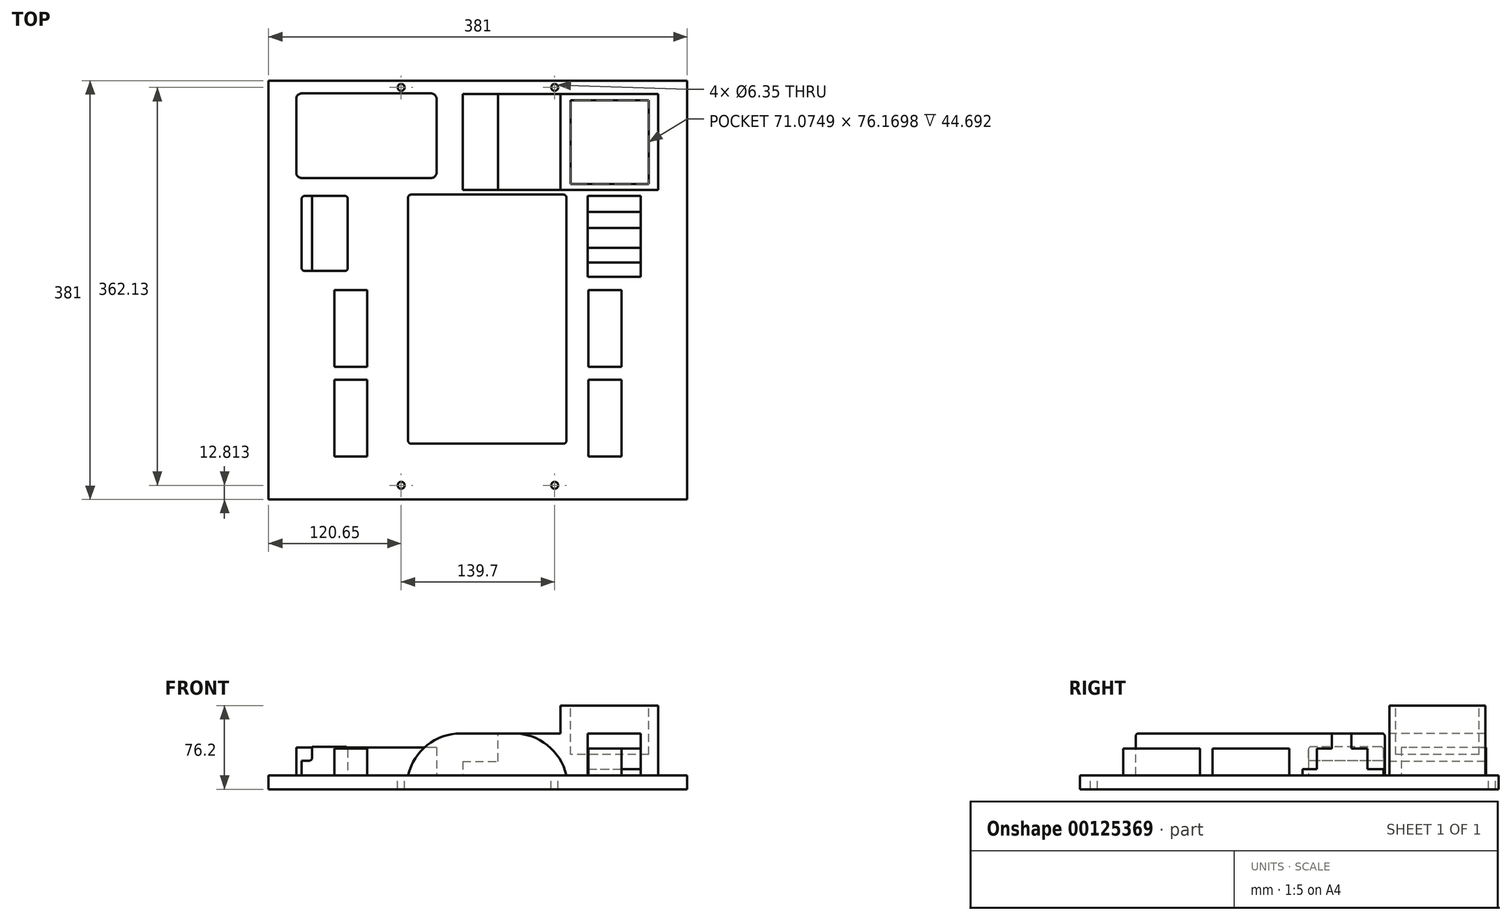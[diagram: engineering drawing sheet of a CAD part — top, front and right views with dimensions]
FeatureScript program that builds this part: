
annotation { "Feature Type Name" : "Feature", "Feature Type Description" : "" }
export const myFeature = defineFeature(function(context is Context, id is Id, definition is map)
    precondition{}
    {
        {
            var Q0;
            Q0=qCreatedBy(makeId("Top.planeOp"),FACE);
            var sketch = newSketch(context, id + "F0", { "sketchPlane" : qUnion([Q0])});
            skLineSegment(sketch, "E0.bottom", {"start": v(190.5, 190.5) * mm, "end": v(-190.5, 190.5) * mm});
            skLineSegment(sketch, "E0.top", {"start": v(190.5, -190.5) * mm, "end": v(-190.5, -190.5) * mm});
            skLineSegment(sketch, "E0.left", {"start": v(190.5, 190.5) * mm, "end": v(190.5, -190.5) * mm});
            skLineSegment(sketch, "E0.right", {"start": v(-190.5, 190.5) * mm, "end": v(-190.5, -190.5) * mm});
            skPoint(sketch, "E0.middle", {"position": v(0, 0) * mm});
            skSolve(sketch);
        }
        {
            var Q0;
            Q0=makeQuery(id+"F0.imprint","IMPRINT",FACE,{"disambiguationData":[TD([[makeQuery(id+"F0.imprint","IMPRINT",EDGE,{"derivedFrom":sQuery(id+"F0.wireOp",EDGE,"E0.bottom")}),1.0]])]});
            extrude(context, id + "F1", {"entities" : qUnion([Q0]), "depth" : 12.7 * mm});
        }
        {
            var Q0;
            Q0=makeQuery(id+"F1.opExtrude","CAP_FACE",FACE,{"disambiguationData":[OSD([sQuery(id+"F0.wireOp",EDGE,"E0.bottom"),sQuery(id+"F0.wireOp",EDGE,"E0.top"),sQuery(id+"F0.wireOp",EDGE,"E0.left"),sQuery(id+"F0.wireOp",EDGE,"E0.right")])],"isStart":false});
            var sketch = newSketch(context, id + "F2", { "sketchPlane" : qUnion([Q0])});
            skSolve(sketch);
        }
        {
            var Q0;
            Q0=makeQuery(id+"F2.imprint","IMPRINT",FACE,{"disambiguationData":[TD([[makeQuery(id+"F2.imprint","IMPRINT",EDGE,{"derivedFrom":makeQuery(id+"F1.opExtrude","CAP_EDGE",EDGE,{"disambiguationData":[OSD([sQuery(id+"F0.wireOp",EDGE,"E0.bottom")])],"isStart":false})}),1.0]])]});
            var sketch = newSketch(context, id + "F3", { "sketchPlane" : qUnion([Q0])});
            skLineSegment(sketch, "E1.bottom", {"start": v(-63.5, -139.7) * mm, "end": v(80.52, -139.7) * mm});
            skLineSegment(sketch, "E1.top", {"start": v(-63.5, 86.87) * mm, "end": v(80.52, 86.87) * mm});
            skLineSegment(sketch, "E1.left", {"start": v(-63.5, -139.7) * mm, "end": v(-63.5, 86.87) * mm});
            skLineSegment(sketch, "E1.right", {"start": v(80.52, -139.7) * mm, "end": v(80.52, 86.87) * mm});
            skSolve(sketch);
        }
        {
            var Q0;
            Q0=makeQuery(id+"F3.imprint","IMPRINT",FACE,{"disambiguationData":[TD([[makeQuery(id+"F3.imprint","IMPRINT",EDGE,{"derivedFrom":sQuery(id+"F3.wireOp",EDGE,"E1.bottom")}),1.0]])]});
            extrude(context, id + "F4", {"entities" : qUnion([Q0]), "operationType" : NewBodyOperationType.ADD, "depth" : 38.1 * mm});
        }
        {
            var Q0;
            Q0=makeQuery(id+"F2.imprint","IMPRINT",FACE,{"disambiguationData":[TD([[makeQuery(id+"F2.imprint","IMPRINT",EDGE,{"derivedFrom":makeQuery(id+"F1.opExtrude","CAP_EDGE",EDGE,{"disambiguationData":[OSD([sQuery(id+"F0.wireOp",EDGE,"E0.bottom")])],"isStart":false})}),1.0]])]});
            var sketch = newSketch(context, id + "F5", { "sketchPlane" : qUnion([Q0])});
            skLineSegment(sketch, "E2.bottom", {"start": v(-13.9, 178.37) * mm, "end": v(164.16, 178.37) * mm});
            skLineSegment(sketch, "E2.top", {"start": v(-13.9, 91) * mm, "end": v(164.16, 91) * mm});
            skLineSegment(sketch, "E2.left", {"start": v(-13.9, 178.37) * mm, "end": v(-13.9, 91) * mm});
            skLineSegment(sketch, "E2.right", {"start": v(164.16, 178.37) * mm, "end": v(164.16, 91) * mm});
            skSolve(sketch);
        }
        {
            var Q0;
            Q0 = qSketchRegion(id + "F5", true);
            extrude(context, id + "F6", {"entities" : qUnion([Q0]), "operationType" : NewBodyOperationType.ADD, "depth" : 63.5 * mm});
        }
        {
            var Q0;
            Q0=makeQuery(id+"F2.imprint","IMPRINT",FACE,{"disambiguationData":[TD([[makeQuery(id+"F2.imprint","IMPRINT",EDGE,{"derivedFrom":makeQuery(id+"F1.opExtrude","CAP_EDGE",EDGE,{"disambiguationData":[OSD([sQuery(id+"F0.wireOp",EDGE,"E0.bottom")])],"isStart":false})}),1.0]])]});
            var sketch = newSketch(context, id + "F7", { "sketchPlane" : qUnion([Q0])});
            skLineSegment(sketch, "E3.bottom", {"start": v(-37.6, 178.96) * mm, "end": v(-165.35, 178.96) * mm});
            skLineSegment(sketch, "E3.top", {"start": v(-37.6, 102) * mm, "end": v(-165.35, 102) * mm});
            skLineSegment(sketch, "E3.left", {"start": v(-37.6, 178.96) * mm, "end": v(-37.6, 102) * mm});
            skLineSegment(sketch, "E3.right", {"start": v(-165.35, 178.96) * mm, "end": v(-165.35, 102) * mm});
            skSolve(sketch);
        }
        {
            var Q0;
            Q0 = qSketchRegion(id + "F7", true);
            extrude(context, id + "F8", {"entities" : qUnion([Q0]), "operationType" : NewBodyOperationType.ADD, "depth" : 25.15 * mm});
        }
        {
            var Q0;
            Q0=makeQuery(id+"F2.imprint","IMPRINT",FACE,{"disambiguationData":[TD([[makeQuery(id+"F2.imprint","IMPRINT",EDGE,{"derivedFrom":makeQuery(id+"F1.opExtrude","CAP_EDGE",EDGE,{"disambiguationData":[OSD([sQuery(id+"F0.wireOp",EDGE,"E0.bottom")])],"isStart":false})}),1.0]])]});
            var sketch = newSketch(context, id + "F9", { "sketchPlane" : qUnion([Q0])});
            skLineSegment(sketch, "E4.bottom", {"start": v(-160.35, 85.65) * mm, "end": v(-118.44, 85.65) * mm});
            skLineSegment(sketch, "E4.top", {"start": v(-160.35, 17.48) * mm, "end": v(-118.44, 17.48) * mm});
            skLineSegment(sketch, "E4.left", {"start": v(-160.35, 85.65) * mm, "end": v(-160.35, 17.48) * mm});
            skLineSegment(sketch, "E4.right", {"start": v(-118.44, 85.65) * mm, "end": v(-118.44, 17.48) * mm});
            skSolve(sketch);
        }
        {
            var Q0;
            Q0 = qSketchRegion(id + "F9", true);
            extrude(context, id + "F10", {"entities" : qUnion([Q0]), "operationType" : NewBodyOperationType.ADD, "depth" : 26.03 * mm});
        }
        {
            var Q0;
            Q0=makeQuery(id+"F2.imprint","IMPRINT",FACE,{"disambiguationData":[TD([[makeQuery(id+"F2.imprint","IMPRINT",EDGE,{"derivedFrom":makeQuery(id+"F1.opExtrude","CAP_EDGE",EDGE,{"disambiguationData":[OSD([sQuery(id+"F0.wireOp",EDGE,"E0.bottom")])],"isStart":false})}),1.0]])]});
            var sketch = newSketch(context, id + "F11", { "sketchPlane" : qUnion([Q0])});
            skLineSegment(sketch, "E5.bottom", {"start": v(99.83, 85.66) * mm, "end": v(148, 85.66) * mm});
            skLineSegment(sketch, "E5.top", {"start": v(99.83, 12) * mm, "end": v(148, 12) * mm});
            skLineSegment(sketch, "E5.left", {"start": v(99.83, 85.66) * mm, "end": v(99.83, 12) * mm});
            skLineSegment(sketch, "E5.right", {"start": v(148, 85.66) * mm, "end": v(148, 12) * mm});
            skSolve(sketch);
        }
        {
            var Q0;
            Q0 = qSketchRegion(id + "F11", true);
            extrude(context, id + "F12", {"entities" : qUnion([Q0]), "operationType" : NewBodyOperationType.ADD, "depth" : 38.1 * mm});
        }
        {
            var Q0;
            Q0=makeQuery(id+"F2.imprint","IMPRINT",FACE,{"disambiguationData":[TD([[makeQuery(id+"F2.imprint","IMPRINT",EDGE,{"derivedFrom":makeQuery(id+"F1.opExtrude","CAP_EDGE",EDGE,{"disambiguationData":[OSD([sQuery(id+"F0.wireOp",EDGE,"E0.bottom")])],"isStart":false})}),1.0]])]});
            var sketch = newSketch(context, id + "F13", { "sketchPlane" : qUnion([Q0])});
            skLineSegment(sketch, "E6.bottom", {"start": v(-130.73, 0) * mm, "end": v(-100.64, 0) * mm});
            skLineSegment(sketch, "E6.top", {"start": v(-130.73, -69.85) * mm, "end": v(-100.64, -69.85) * mm});
            skLineSegment(sketch, "E6.left", {"start": v(-130.73, 0) * mm, "end": v(-130.73, -69.85) * mm});
            skLineSegment(sketch, "E6.right", {"start": v(-100.64, 0) * mm, "end": v(-100.64, -69.85) * mm});
            skLineSegment(sketch, "E7.bottom", {"start": v(-130.73, -81.45) * mm, "end": v(-100.64, -81.45) * mm});
            skLineSegment(sketch, "E7.top", {"start": v(-130.73, -151.3) * mm, "end": v(-100.64, -151.3) * mm});
            skLineSegment(sketch, "E7.left", {"start": v(-130.73, -81.45) * mm, "end": v(-130.73, -151.3) * mm});
            skLineSegment(sketch, "E7.right", {"start": v(-100.64, -81.45) * mm, "end": v(-100.64, -151.3) * mm});
            skLineSegment(sketch, "E8.MirrorCS", {"start": v(100.64, 0) * mm, "end": v(100.64, -69.85) * mm});
            skLineSegment(sketch, "E9.MirrorCS", {"start": v(130.73, 0) * mm, "end": v(100.64, 0) * mm});
            skLineSegment(sketch, "E10.MirrorCS", {"start": v(130.73, 0) * mm, "end": v(130.73, -69.85) * mm});
            skLineSegment(sketch, "E11.MirrorCS", {"start": v(130.73, -69.85) * mm, "end": v(100.64, -69.85) * mm});
            skLineSegment(sketch, "E12.MirrorCS", {"start": v(130.73, -81.45) * mm, "end": v(100.64, -81.45) * mm});
            skLineSegment(sketch, "E13.MirrorCS", {"start": v(130.73, -81.45) * mm, "end": v(130.73, -151.3) * mm});
            skLineSegment(sketch, "E14.MirrorCS", {"start": v(130.73, -151.3) * mm, "end": v(100.64, -151.3) * mm});
            skLineSegment(sketch, "E15.MirrorCS", {"start": v(100.64, -81.45) * mm, "end": v(100.64, -151.3) * mm});
            skSolve(sketch);
        }
        {
            var Q0;
            Q0 = qSketchRegion(id + "F13", true);
            extrude(context, id + "F14", {"entities" : qUnion([Q0]), "operationType" : NewBodyOperationType.ADD, "depth" : 24.38 * mm});
        }
        {
            var Q0;
            Q0=makeQuery(id+"F4.opExtrude","CAP_EDGE",EDGE,{"disambiguationData":[OSD([sQuery(id+"F3.wireOp",EDGE,"E1.right")])],"isStart":false});
            var Q1;
            Q1=makeQuery(id+"F4.opExtrude","CAP_EDGE",EDGE,{"disambiguationData":[OSD([sQuery(id+"F3.wireOp",EDGE,"E1.left")])],"isStart":false});
            fillet(context, id + "F15", {"entities" : qUnion([Q0, Q1]), "radius" : 49.26 * mm, "tangentPropagation" : true, "allowEdgeOverflow" : false});
        }
        {
            var Q0;
            Q0=makeQuery(id+"F6.opExtrude","CAP_FACE",FACE,{"disambiguationData":[OSD([sQuery(id+"F5.wireOp",EDGE,"E2.bottom"),sQuery(id+"F5.wireOp",EDGE,"E2.top"),sQuery(id+"F5.wireOp",EDGE,"E2.left"),sQuery(id+"F5.wireOp",EDGE,"E2.right")])],"isStart":false});
            var sketch = newSketch(context, id + "F16", { "sketchPlane" : qUnion([Q0])});
            skLineSegment(sketch, "E16.bottom", {"start": v(155.35, 172.85) * mm, "end": v(84.27, 172.85) * mm});
            skLineSegment(sketch, "E16.top", {"start": v(155.35, 96.68) * mm, "end": v(84.27, 96.68) * mm});
            skLineSegment(sketch, "E16.left", {"start": v(155.35, 172.85) * mm, "end": v(155.35, 96.68) * mm});
            skLineSegment(sketch, "E16.right", {"start": v(84.27, 172.85) * mm, "end": v(84.27, 96.68) * mm});
            skSolve(sketch);
        }
        {
            var Q0;
            Q0=makeQuery(id+"F16.imprint","IMPRINT",FACE,{"disambiguationData":[TD([[makeQuery(id+"F16.imprint","IMPRINT",EDGE,{"derivedFrom":sQuery(id+"F16.wireOp",EDGE,"E16.bottom")}),1.0]])]});
            extrude(context, id + "F17", {"entities" : qUnion([Q0]), "operationType" : NewBodyOperationType.REMOVE, "oppositeDirection" : true, "depth" : 44.7 * mm});
        }
        {
            var Q0;
            Q0=makeQuery(id+"F6.opExtrude","CAP_FACE",FACE,{"disambiguationData":[OSD([sQuery(id+"F5.wireOp",EDGE,"E2.bottom"),sQuery(id+"F5.wireOp",EDGE,"E2.top"),sQuery(id+"F5.wireOp",EDGE,"E2.left"),sQuery(id+"F5.wireOp",EDGE,"E2.right")])],"isStart":false});
            var sketch = newSketch(context, id + "F18", { "sketchPlane" : qUnion([Q0])});
            skLineSegment(sketch, "E17.bottom", {"start": v(75.14, 178.37) * mm, "end": v(-13.9, 178.37) * mm});
            skLineSegment(sketch, "E17.top", {"start": v(75.14, 91) * mm, "end": v(-13.9, 91) * mm});
            skLineSegment(sketch, "E17.left", {"start": v(75.14, 178.37) * mm, "end": v(75.14, 91) * mm});
            skLineSegment(sketch, "E17.right", {"start": v(-13.9, 178.37) * mm, "end": v(-13.9, 91) * mm});
            skSolve(sketch);
        }
        {
            var Q0;
            Q0=makeQuery(id+"F18.imprint","IMPRINT",FACE,{"disambiguationData":[TD([[makeQuery(id+"F18.imprint","IMPRINT",EDGE,{"derivedFrom":sQuery(id+"F18.wireOp",EDGE,"E17.bottom")}),-1.0]])]});
            extrude(context, id + "F19", {"entities" : qUnion([Q0]), "operationType" : NewBodyOperationType.REMOVE, "oppositeDirection" : true, "depth" : 25.4 * mm});
        }
        {
            var Q0;
            Q0=makeQuery(id+"F19.boolean.opBoolean","COPY",FACE,{"derivedFrom":makeQuery(id+"F19.opExtrude","CAP_FACE",FACE,{"disambiguationData":[OSD([sQuery(id+"F18.wireOp",EDGE,"E17.bottom"),sQuery(id+"F18.wireOp",EDGE,"E17.top"),sQuery(id+"F18.wireOp",EDGE,"E17.left"),sQuery(id+"F18.wireOp",EDGE,"E17.right")])],"isStart":false})});
            var sketch = newSketch(context, id + "F20", { "sketchPlane" : qUnion([Q0])});
            skLineSegment(sketch, "E18.bottom", {"start": v(-13.9, 178.37) * mm, "end": v(18.28, 178.37) * mm});
            skLineSegment(sketch, "E18.top", {"start": v(-13.9, 91) * mm, "end": v(18.28, 91) * mm});
            skLineSegment(sketch, "E18.left", {"start": v(-13.9, 178.37) * mm, "end": v(-13.9, 91) * mm});
            skLineSegment(sketch, "E18.right", {"start": v(18.28, 178.37) * mm, "end": v(18.28, 91) * mm});
            skSolve(sketch);
        }
        {
            var Q0;
            Q0=makeQuery(id+"F20.imprint","IMPRINT",FACE,{"disambiguationData":[TD([[makeQuery(id+"F20.imprint","IMPRINT",EDGE,{"derivedFrom":sQuery(id+"F20.wireOp",EDGE,"E18.bottom")}),-1.0]])]});
            extrude(context, id + "F21", {"entities" : qUnion([Q0]), "operationType" : NewBodyOperationType.REMOVE, "oppositeDirection" : true, "depth" : 25.4 * mm});
        }
        {
            var Q0;
            Q0=makeQuery(id+"F12.opExtrude","CAP_FACE",FACE,{"disambiguationData":[OSD([sQuery(id+"F11.wireOp",EDGE,"E5.bottom"),sQuery(id+"F11.wireOp",EDGE,"E5.top"),sQuery(id+"F11.wireOp",EDGE,"E5.left"),sQuery(id+"F11.wireOp",EDGE,"E5.right")])],"isStart":false});
            var sketch = newSketch(context, id + "F22", { "sketchPlane" : qUnion([Q0])});
            skLineSegment(sketch, "E19.bottom", {"start": v(99.83, 56.58) * mm, "end": v(148, 56.58) * mm});
            skLineSegment(sketch, "E19.top", {"start": v(99.83, 85.66) * mm, "end": v(148, 85.66) * mm});
            skLineSegment(sketch, "E19.left", {"start": v(99.83, 56.58) * mm, "end": v(99.83, 85.66) * mm});
            skLineSegment(sketch, "E19.right", {"start": v(148, 56.58) * mm, "end": v(148, 85.66) * mm});
            skLineSegment(sketch, "E20.bottom", {"start": v(99.83, 38.58) * mm, "end": v(148, 38.58) * mm});
            skLineSegment(sketch, "E20.top", {"start": v(99.83, 12) * mm, "end": v(148, 12) * mm});
            skLineSegment(sketch, "E20.left", {"start": v(99.83, 38.58) * mm, "end": v(99.83, 12) * mm});
            skLineSegment(sketch, "E20.right", {"start": v(148, 38.58) * mm, "end": v(148, 12) * mm});
            skSolve(sketch);
        }
        {
            var Q0;
            Q0=makeQuery(id+"F22.imprint","IMPRINT",FACE,{"disambiguationData":[TD([[makeQuery(id+"F22.imprint","IMPRINT",EDGE,{"derivedFrom":sQuery(id+"F22.wireOp",EDGE,"E19.bottom")}),1.0]])]});
            var Q1;
            Q1=makeQuery(id+"F22.imprint","IMPRINT",FACE,{"disambiguationData":[TD([[makeQuery(id+"F22.imprint","IMPRINT",EDGE,{"derivedFrom":sQuery(id+"F22.wireOp",EDGE,"E20.bottom")}),-1.0]])]});
            extrude(context, id + "F23", {"entities" : qUnion([Q0, Q1]), "operationType" : NewBodyOperationType.REMOVE, "oppositeDirection" : true, "depth" : 13.65 * mm});
        }
        {
            var Q0;
            Q0=makeQuery(id+"F23.boolean.opBoolean","COPY",FACE,{"derivedFrom":makeQuery(id+"F23.opExtrude","CAP_FACE",FACE,{"disambiguationData":[OSD([sQuery(id+"F22.wireOp",EDGE,"E19.bottom"),sQuery(id+"F22.wireOp",EDGE,"E19.top"),sQuery(id+"F22.wireOp",EDGE,"E19.left"),sQuery(id+"F22.wireOp",EDGE,"E19.right")])],"isStart":false})});
            var sketch = newSketch(context, id + "F24", { "sketchPlane" : qUnion([Q0])});
            skLineSegment(sketch, "E21.bottom", {"start": v(99.83, 85.66) * mm, "end": v(148, 85.66) * mm});
            skLineSegment(sketch, "E21.top", {"start": v(99.83, 71.12) * mm, "end": v(148, 71.12) * mm});
            skLineSegment(sketch, "E21.left", {"start": v(99.83, 85.66) * mm, "end": v(99.83, 71.12) * mm});
            skLineSegment(sketch, "E21.right", {"start": v(148, 85.66) * mm, "end": v(148, 71.12) * mm});
            skLineSegment(sketch, "E22.bottom", {"start": v(148, 10.9) * mm, "end": v(99.83, 10.9) * mm});
            skLineSegment(sketch, "E22.top", {"start": v(148, 25.2) * mm, "end": v(99.83, 25.2) * mm});
            skLineSegment(sketch, "E22.left", {"start": v(148, 10.9) * mm, "end": v(148, 25.2) * mm});
            skLineSegment(sketch, "E22.right", {"start": v(99.83, 10.9) * mm, "end": v(99.83, 25.2) * mm});
            skSolve(sketch);
        }
        {
            var Q0;
            Q0=makeQuery(id+"F24.imprint","IMPRINT",FACE,{"disambiguationData":[TD([[makeQuery(id+"F24.imprint","IMPRINT",EDGE,{"derivedFrom":sQuery(id+"F24.wireOp",EDGE,"E21.bottom")}),-1.0]])]});
            var Q1;
            Q1=makeQuery(id+"F24.imprint","IMPRINT",FACE,{"disambiguationData":[TD([[makeQuery(id+"F24.imprint","IMPRINT",EDGE,{"derivedFrom":sQuery(id+"F24.wireOp",EDGE,"E22.bottom")}),-1.0]])]});
            extrude(context, id + "F25", {"entities" : qUnion([Q0, Q1]), "operationType" : NewBodyOperationType.REMOVE, "oppositeDirection" : true, "depth" : 18.87 * mm});
        }
        {
            var Q0;
            Q0=makeQuery(id+"F10.opExtrude","CAP_FACE",FACE,{"disambiguationData":[OSD([sQuery(id+"F9.wireOp",EDGE,"E4.bottom"),sQuery(id+"F9.wireOp",EDGE,"E4.top"),sQuery(id+"F9.wireOp",EDGE,"E4.left"),sQuery(id+"F9.wireOp",EDGE,"E4.right")])],"isStart":false});
            var sketch = newSketch(context, id + "F26", { "sketchPlane" : qUnion([Q0])});
            skLineSegment(sketch, "E23", {"start": v(-150.9, 85.65) * mm, "end": v(-150.9, 17.48) * mm});
            skSolve(sketch);
        }
        {
            var Q0;
            {var subQ0=sQuery(id+"F26.wireOp",EDGE,"E23");Q0=makeQuery(id+"F26.imprint","IMPRINT",FACE,{"disambiguationData":[TD([[makeQuery(id+"F26.imprint","IMPRINT",EDGE,{"derivedFrom":subQ0}),-1.0]])]});}
            extrude(context, id + "F27", {"entities" : qUnion([Q0]), "operationType" : NewBodyOperationType.REMOVE, "oppositeDirection" : true, "depth" : 12.7 * mm});
        }
        {
            var Q0;
            Q0=makeQuery(id+"F27.boolean.opBoolean","COPY",EDGE,{"derivedFrom":makeQuery(id+"F27.opExtrude","CAP_EDGE",EDGE,{"disambiguationData":[OSD([sQuery(id+"F26.wireOp",EDGE,"E23")])],"isStart":false})});
            var Q1;
            Q1=makeQuery(id+"F27.boolean.opBoolean","COPY",EDGE,{"derivedFrom":makeQuery(id+"F27.opExtrude","CAP_EDGE",EDGE,{"disambiguationData":[OSD([sQuery(id+"F9.wireOp",EDGE,"E4.left")])],"isStart":false})});
            var Q2;
            Q2=makeQuery(id+"F27.boolean.opBoolean","COPY",EDGE,{"derivedFrom":makeQuery(id+"F27.opExtrude","CAP_EDGE",EDGE,{"disambiguationData":[OSD([sQuery(id+"F26.wireOp",EDGE,"E23")])],"isStart":true})});
            var Q3;
            Q3=makeQuery(id+"F10.opExtrude","CAP_EDGE",EDGE,{"disambiguationData":[OSD([sQuery(id+"F9.wireOp",EDGE,"E4.top")])],"isStart":false});
            var Q4;
            Q4=makeQuery(id+"F10.opExtrude","CAP_EDGE",EDGE,{"disambiguationData":[OSD([sQuery(id+"F9.wireOp",EDGE,"E4.right")])],"isStart":false});
            var Q5;
            Q5=makeQuery(id+"F10.opExtrude","CAP_EDGE",EDGE,{"disambiguationData":[OSD([sQuery(id+"F9.wireOp",EDGE,"E4.bottom")])],"isStart":false});
            var Q6;
            Q6=makeQuery(id+"F10.opExtrude","SWEPT_EDGE",EDGE,{"disambiguationData":[OSD([sQuery(id+"F9.wireOp",EDGE,"E4.top"),sQuery(id+"F9.wireOp",EDGE,"E4.right")])]});
            var Q7;
            Q7=makeQuery(id+"F4.opExtrude","CAP_FACE",FACE,{"disambiguationData":[OSD([sQuery(id+"F3.wireOp",EDGE,"E1.bottom"),sQuery(id+"F3.wireOp",EDGE,"E1.top"),sQuery(id+"F3.wireOp",EDGE,"E1.left"),sQuery(id+"F3.wireOp",EDGE,"E1.right")])],"isStart":false});
            var Q8;
            Q8=makeQuery(id+"F10.opExtrude","SWEPT_EDGE",EDGE,{"disambiguationData":[OSD([sQuery(id+"F9.wireOp",EDGE,"E4.top"),sQuery(id+"F9.wireOp",EDGE,"E4.left")])]});
            var Q9;
            Q9=makeQuery(id+"F10.opExtrude","SWEPT_EDGE",EDGE,{"disambiguationData":[OSD([sQuery(id+"F9.wireOp",EDGE,"E4.bottom"),sQuery(id+"F9.wireOp",EDGE,"E4.left")])]});
            var Q10;
            Q10=makeQuery(id+"F10.opExtrude","SWEPT_EDGE",EDGE,{"disambiguationData":[OSD([sQuery(id+"F9.wireOp",EDGE,"E4.bottom"),sQuery(id+"F9.wireOp",EDGE,"E4.right")])]});
            fillet(context, id + "F28", {"entities" : qUnion([Q0, Q1, Q2, Q3, Q4, Q5, Q6, Q7, Q8, Q9, Q10]), "radius" : 2.54 * mm, "tangentPropagation" : true, "allowEdgeOverflow" : false});
        }
        {
            var Q0;
            Q0=makeQuery(id+"F2.imprint","IMPRINT",FACE,{"disambiguationData":[TD([[makeQuery(id+"F2.imprint","IMPRINT",EDGE,{"derivedFrom":makeQuery(id+"F1.opExtrude","CAP_EDGE",EDGE,{"disambiguationData":[OSD([sQuery(id+"F0.wireOp",EDGE,"E0.bottom")])],"isStart":false})}),1.0]])]});
            var sketch = newSketch(context, id + "F29", { "sketchPlane" : qUnion([Q0])});
            skPoint(sketch, "E24", {"position": v(-69.85, -177.69) * mm});
            skPoint(sketch, "E25", {"position": v(69.85, -177.69) * mm});
            skPoint(sketch, "E26", {"position": v(-69.85, 184.44) * mm});
            skPoint(sketch, "E27", {"position": v(69.85, 184.44) * mm});
            skSolve(sketch);
        }
        {
            var Q0;
            Q0=sQuery(id+"F29.wireOp",VERTEX,"E24");
            var Q1;
            Q1=sQuery(id+"F29.wireOp",VERTEX,"E25");
            var Q2;
            Q2=sQuery(id+"F29.wireOp",VERTEX,"E27");
            var Q3;
            Q3=sQuery(id+"F29.wireOp",VERTEX,"E26");
            var Q4;
            Q4=makeQuery(id+"F1.opExtrude","SWEPT_BODY",BODY,{"disambiguationData":[OSD([sQuery(id+"F0.wireOp",EDGE,"E0.bottom"),sQuery(id+"F0.wireOp",EDGE,"E0.top"),sQuery(id+"F0.wireOp",EDGE,"E0.left"),sQuery(id+"F0.wireOp",EDGE,"E0.right")])]});
            hole(context, id + "F30", {"style" : HoleStyle.SIMPLE, "endStyle" : HoleEndStyle.THROUGH, "holeDiameter" : 6.35 * mm, "locations" : qUnion([Q0, Q1, Q2, Q3]), "scope" : qUnion([Q4]), "isTappedThrough" : true});
        }
        {
            var Q0;
            Q0=makeQuery(id+"F8.opExtrude","SWEPT_EDGE",EDGE,{"disambiguationData":[OSD([sQuery(id+"F7.wireOp",EDGE,"E3.top"),sQuery(id+"F7.wireOp",EDGE,"E3.left")])]});
            var Q1;
            Q1=makeQuery(id+"F8.opExtrude","SWEPT_EDGE",EDGE,{"disambiguationData":[OSD([sQuery(id+"F7.wireOp",EDGE,"E3.top"),sQuery(id+"F7.wireOp",EDGE,"E3.right")])]});
            var Q2;
            Q2=makeQuery(id+"F8.opExtrude","SWEPT_EDGE",EDGE,{"disambiguationData":[OSD([sQuery(id+"F7.wireOp",EDGE,"E3.bottom"),sQuery(id+"F7.wireOp",EDGE,"E3.right")])]});
            var Q3;
            Q3=makeQuery(id+"F8.opExtrude","SWEPT_EDGE",EDGE,{"disambiguationData":[OSD([sQuery(id+"F7.wireOp",EDGE,"E3.bottom"),sQuery(id+"F7.wireOp",EDGE,"E3.left")])]});
            fillet(context, id + "F31", {"entities" : qUnion([Q0, Q1, Q2, Q3]), "radius" : 5.08 * mm, "tangentPropagation" : true, "allowEdgeOverflow" : false});
        }
    });
